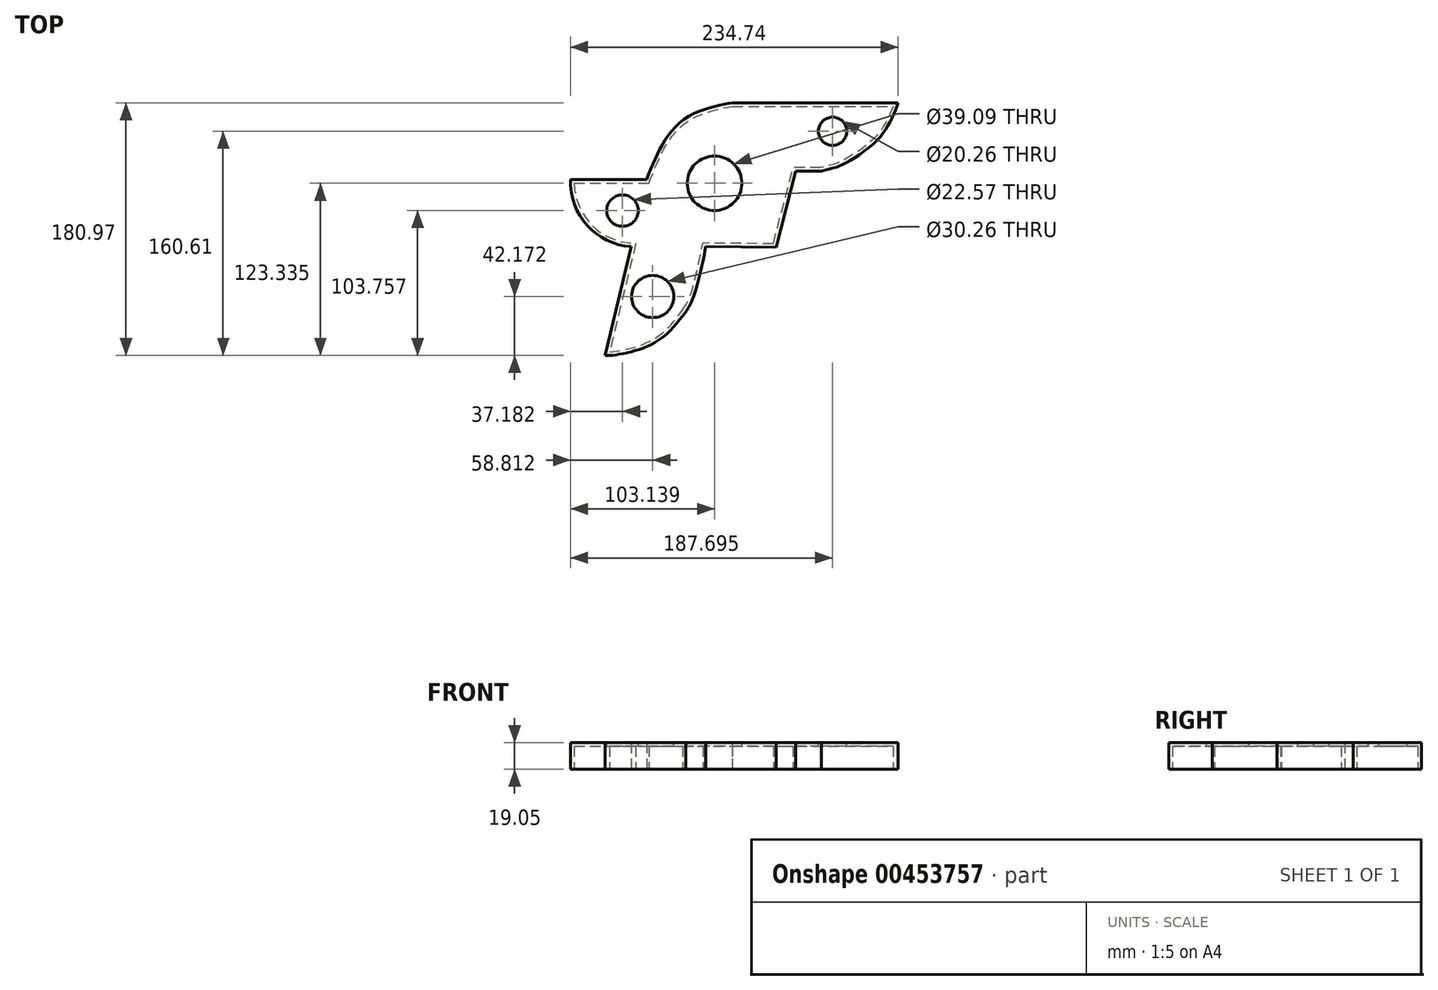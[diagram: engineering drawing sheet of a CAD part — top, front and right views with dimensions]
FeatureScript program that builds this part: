
annotation { "Feature Type Name" : "Feature", "Feature Type Description" : "" }
export const myFeature = defineFeature(function(context is Context, id is Id, definition is map)
    precondition{}
    {
        {
            var Q0;
            Q0=qCreatedBy(makeId("Top.planeOp"),FACE);
            var sketch = newSketch(context, id + "F0", { "sketchPlane" : qUnion([Q0])});
            skLineSegment(sketch, "E0", {"start": v(54.88, 12.45) * mm, "end": v(68.98, 66.96) * mm});
            skLineSegment(sketch, "E1", {"start": v(54.88, 12.45) * mm, "end": v(4.6, 12.92) * mm});
            skArc(sketch, "E2", {"start": v(-92.26, 61.14) * mm, "mid": v(-80.39, 28.14) * mm, "end": v(-48.8, 12.92) * mm});
            skFitSpline(sketch, "E3", {"points": [v(-67.63, -64.9) * mm, v(-62.67, -64.9) * mm, v(-51.38, -62.98) * mm, v(-38.17, -58.85) * mm, v(-22.75, -48.94) * mm, v(-9.81, -33.8) * mm], "startDerivative": vector(36.09, -1.9) * mm, "endDerivative": vector(48.8, 65.1) * mm});
            skFitSpline(sketch, "E4", {"points": [v(-9.81, -33.8) * mm, v(-4.58, -24.16) * mm, v(4.6, 12.92) * mm], "startDerivative": vector(15.15, 22.5) * mm, "endDerivative": vector(13.83, 66.49) * mm});
            skLineSegment(sketch, "E5", {"start": v(-48.8, 12.92) * mm, "end": v(-67.63, -64.9) * mm});
            skLineSegment(sketch, "E6", {"start": v(-92.26, 61.14) * mm, "end": v(-37.9, 61.14) * mm});
            skFitSpline(sketch, "E7", {"points": [v(-37.9, 61.14) * mm, v(-31.84, 75.77) * mm, v(-24.96, 88.71) * mm, v(-14.5, 101.38) * mm, v(0, 109.9) * mm, v(14.41, 114.31) * mm, v(23.5, 115.97) * mm], "startDerivative": vector(34.01, 85.95) * mm, "endDerivative": vector(64.53, 10.2) * mm});
            skLineSegment(sketch, "E8", {"start": v(23.5, 115.97) * mm, "end": v(142.43, 115.97) * mm});
            skFitSpline(sketch, "E9", {"points": [v(142.43, 115.97) * mm, v(136.37, 101.93) * mm, v(124.53, 86.5) * mm, v(103.61, 72.2) * mm, v(87.37, 66.96) * mm], "startDerivative": vector(-24.47, -65.34) * mm, "endDerivative": vector(-129.35, -34.96) * mm});
            skLineSegment(sketch, "E10", {"start": v(87.37, 66.96) * mm, "end": v(68.98, 66.96) * mm});
            skSolve(sketch);
        }
        {
            var Q0;
            Q0=qSketchRegion(id+"F0",true);
            extrude(context, id + "F1", {"entities" : qUnion([Q0]), "depth" : 19.05 * mm});
        }
        {
            var Q0;
            Q0=makeQuery(id+"F1.opExtrude","CAP_FACE",FACE,{"disambiguationData":[OSD([sQuery(id+"F0.wireOp",EDGE,"E0"),sQuery(id+"F0.wireOp",EDGE,"E1"),sQuery(id+"F0.wireOp",EDGE,"E2"),sQuery(id+"F0.wireOp",EDGE,"E3"),sQuery(id+"F0.wireOp",EDGE,"E4"),sQuery(id+"F0.wireOp",EDGE,"E5"),sQuery(id+"F0.wireOp",EDGE,"E6"),sQuery(id+"F0.wireOp",EDGE,"E7"),sQuery(id+"F0.wireOp",EDGE,"E8"),sQuery(id+"F0.wireOp",EDGE,"E9"),sQuery(id+"F0.wireOp",EDGE,"E10")])],"isStart":true});
            shell(context, id + "F2", {"entities" : qUnion([Q0]), "thickness" : 2.54 * mm});
        }
        {
            var Q0;
            Q0=makeQuery(id+"F1.opExtrude","CAP_FACE",FACE,{"disambiguationData":[OSD([sQuery(id+"F0.wireOp",EDGE,"E0"),sQuery(id+"F0.wireOp",EDGE,"E1"),sQuery(id+"F0.wireOp",EDGE,"E2"),sQuery(id+"F0.wireOp",EDGE,"E3"),sQuery(id+"F0.wireOp",EDGE,"E4"),sQuery(id+"F0.wireOp",EDGE,"E5"),sQuery(id+"F0.wireOp",EDGE,"E6"),sQuery(id+"F0.wireOp",EDGE,"E7"),sQuery(id+"F0.wireOp",EDGE,"E8"),sQuery(id+"F0.wireOp",EDGE,"E9"),sQuery(id+"F0.wireOp",EDGE,"E10")])],"isStart":false});
            var sketch = newSketch(context, id + "F3", { "sketchPlane" : qUnion([Q0])});
            skCircle(sketch, "E11", {"center": v(10.83, 58.34) * mm, "radius": 19.54 * mm});
            skCircle(sketch, "E12", {"center": v(95.39, 95.61) * mm, "radius": 10.13 * mm});
            skCircle(sketch, "E13", {"center": v(-55.13, 38.76) * mm, "radius": 11.28 * mm});
            skCircle(sketch, "E14", {"center": v(-33.5, -22.83) * mm, "radius": 15.13 * mm});
            skSolve(sketch);
        }
        {
            var Q0;
            Q0 = qSketchRegion(id + "F3", true);
            extrude(context, id + "F4", {"entities" : qUnion([Q0]), "operationType" : NewBodyOperationType.REMOVE, "oppositeDirection" : true, "depth" : 25.4 * mm});
        }
    });
